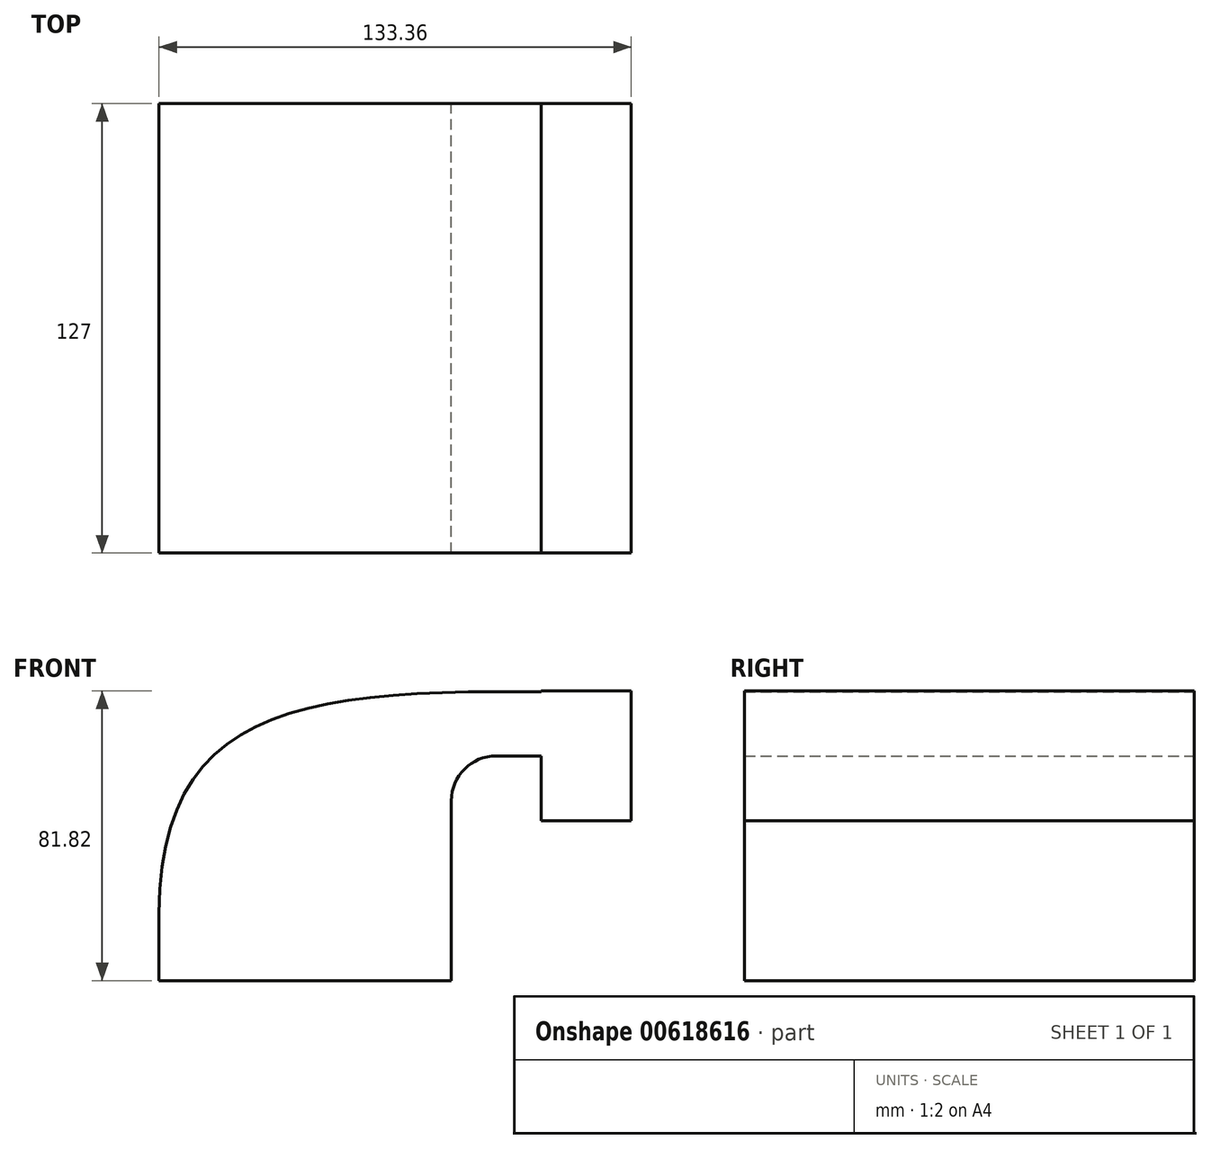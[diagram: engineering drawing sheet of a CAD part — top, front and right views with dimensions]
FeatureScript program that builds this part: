
annotation { "Feature Type Name" : "Feature", "Feature Type Description" : "" }
export const myFeature = defineFeature(function(context is Context, id is Id, definition is map)
    precondition{}
    {
        {
            var Q0;
            Q0=qCreatedBy(makeId("Front.planeOp"),FACE);
            var sketch = newSketch(context, id + "F0", { "sketchPlane" : qUnion([Q0])});
            skLineSegment(sketch, "E0.bottom", {"start": v(41.28, -9.52) * mm, "end": v(-41.28, -9.53) * mm});
            skLineSegment(sketch, "E0.top", {"start": v(41.27, 9.53) * mm, "end": v(-41.28, 9.53) * mm});
            skLineSegment(sketch, "E0.left", {"start": v(41.28, -9.52) * mm, "end": v(41.28, 9.53) * mm});
            skLineSegment(sketch, "E0.right", {"start": v(-41.28, -9.53) * mm, "end": v(-41.28, 9.53) * mm});
            skPoint(sketch, "E0.middle", {"position": v(0, 0) * mm});
            skLineSegment(sketch, "E1.bottom", {"start": v(66.67, 72.29) * mm, "end": v(92.08, 72.29) * mm});
            skLineSegment(sketch, "E1.top", {"start": v(66.67, 35.66) * mm, "end": v(92.08, 35.66) * mm});
            skLineSegment(sketch, "E1.left", {"start": v(66.67, 72.29) * mm, "end": v(66.67, 35.66) * mm});
            skLineSegment(sketch, "E1.right", {"start": v(92.08, 72.29) * mm, "end": v(92.08, 35.66) * mm});
            skPoint(sketch, "E1.middle", {"position": v(79.38, 53.98) * mm});
            skLineSegment(sketch, "E2", {"start": v(41.27, 9.53) * mm, "end": v(41.27, 41.27) * mm});
            skArc(sketch, "E3", {"start": v(41.27, 41.27) * mm, "mid": v(45, 50.26) * mm, "end": v(53.98, 53.98) * mm});
            skLineSegment(sketch, "E4", {"start": v(53.98, 53.98) * mm, "end": v(79.38, 53.98) * mm});
            skLineSegment(sketch, "E5.0", {"start": v(53.98, 72.14) * mm, "end": v(79.38, 72.14) * mm});
            skArc(sketch, "E5.1", {"start": v(23.11, 41.27) * mm, "mid": v(32.15, 63.1) * mm, "end": v(53.98, 72.14) * mm});
            skLineSegment(sketch, "E5.2", {"start": v(23.11, 9.53) * mm, "end": v(23.11, 41.27) * mm});
            skFitSpline(sketch, "E6", {"points": [v(-41.28, 9.53) * mm, v(53.98, 72.14) * mm], "startDerivative": vector(0.97, 162.6) * mm, "endDerivative": vector(180.31, 0.51) * mm});
            skSolve(sketch);
        }
        {
            var Q0;
            Q0 = qSketchRegion(id + "F0", true);
            extrude(context, id + "F1", {"entities" : qUnion([Q0]), "endBound" : BoundingType.SYMMETRIC, "depth" : 127 * mm, "offsetDistance" : 25.4 * mm});
        }
    });
